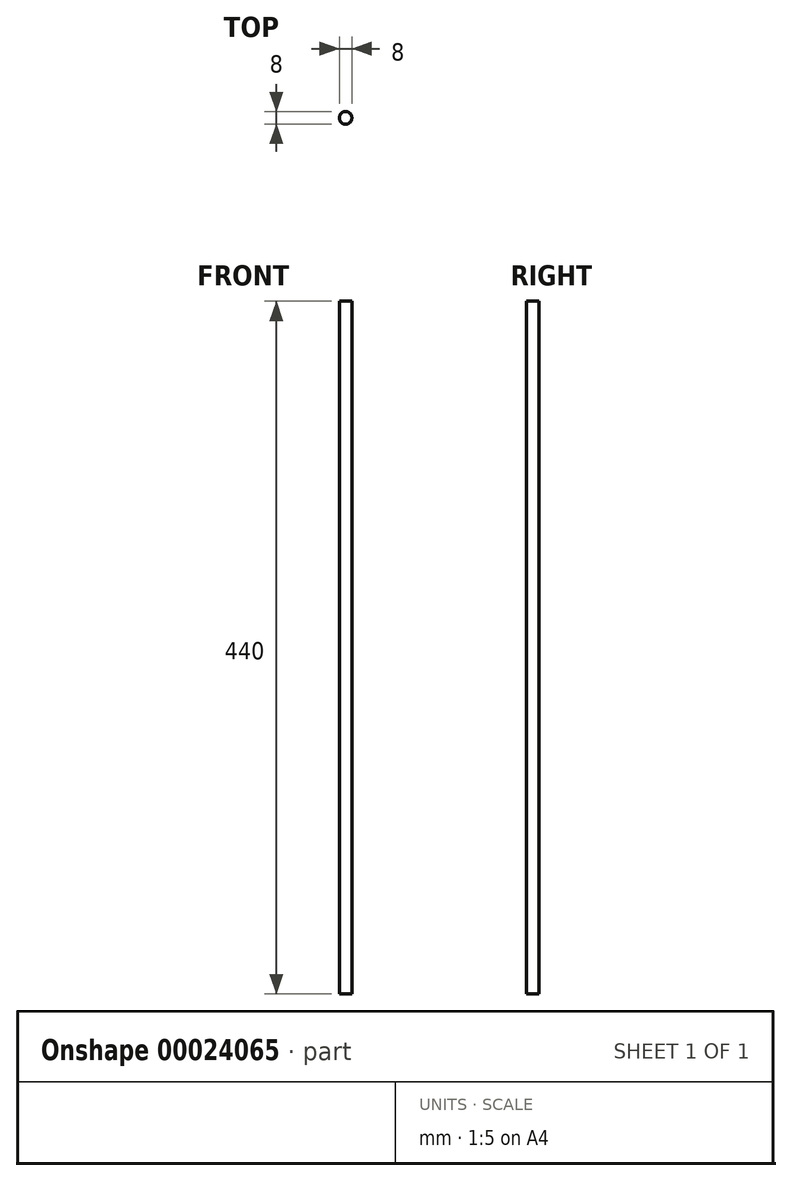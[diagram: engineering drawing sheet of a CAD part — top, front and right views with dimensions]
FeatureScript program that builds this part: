
annotation { "Feature Type Name" : "Feature", "Feature Type Description" : "" }
export const myFeature = defineFeature(function(context is Context, id is Id, definition is map)
    precondition{}
    {
        {
            var Q0;
            Q0=qCreatedBy(makeId("Top.planeOp"),FACE);
            var sketch = newSketch(context, id + "F0", { "sketchPlane" : qUnion([Q0])});
            skCircle(sketch, "E0", {"center": v(0, 0) * mm, "radius": 4 * mm});
            skSolve(sketch);
        }
        {
            var Q0;
            Q0=qSketchRegion(id+"F0",true);
            extrude(context, id + "F1", {"entities" : qUnion([Q0]), "depth" : 440 * mm});
        }
    });
